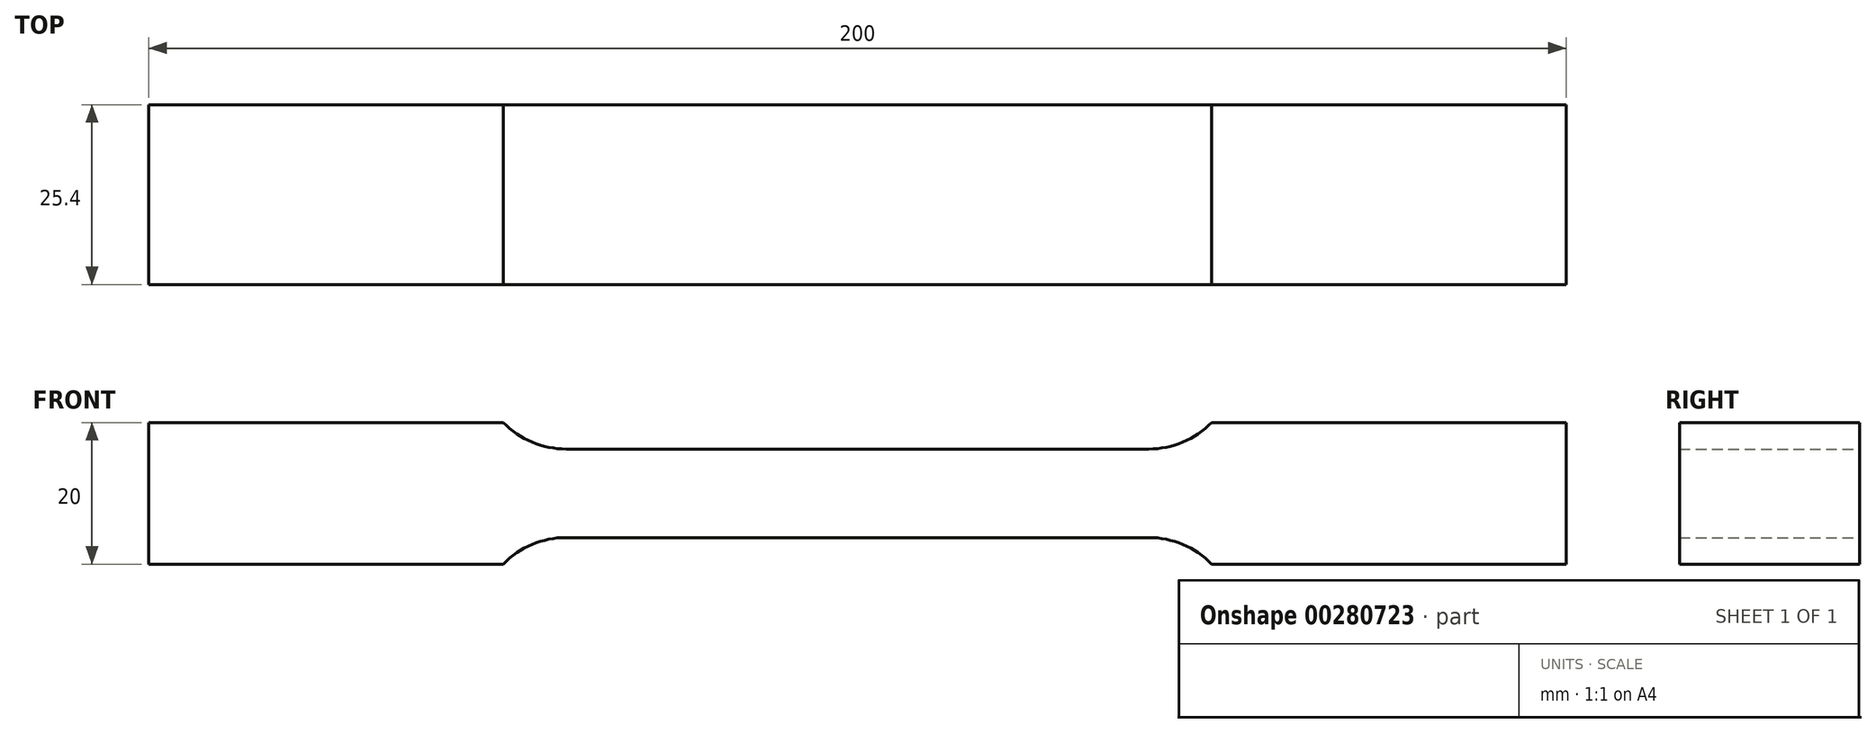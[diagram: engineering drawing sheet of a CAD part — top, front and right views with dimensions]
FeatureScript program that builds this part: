
annotation { "Feature Type Name" : "Feature", "Feature Type Description" : "" }
export const myFeature = defineFeature(function(context is Context, id is Id, definition is map)
    precondition{}
    {
        {
            var Q0;
            Q0=qCreatedBy(makeId("Front.planeOp"),FACE);
            var sketch = newSketch(context, id + "F0", { "sketchPlane" : qUnion([Q0])});
            skLineSegment(sketch, "E0", {"start": v(0, 6.25) * mm, "end": v(41.07, 6.25) * mm});
            skArc(sketch, "E1", {"start": v(41.07, 6.25) * mm, "mid": v(45.91, 7.23) * mm, "end": v(50, 10) * mm});
            skLineSegment(sketch, "E2", {"start": v(50, 10) * mm, "end": v(100, 10) * mm});
            skLineSegment(sketch, "E3.MirrorCS", {"start": v(0, -6.25) * mm, "end": v(41.07, -6.25) * mm});
            skLineSegment(sketch, "E4.MirrorCS", {"start": v(50, -10) * mm, "end": v(100, -10) * mm});
            skArc(sketch, "E5.MirrorCS", {"start": v(41.07, -6.25) * mm, "mid": v(45.91, -7.23) * mm, "end": v(50, -10) * mm});
            skLineSegment(sketch, "E6.MirrorCS", {"start": v(-50, 10) * mm, "end": v(-100, 10) * mm});
            skLineSegment(sketch, "E7.MirrorCS", {"start": v(-50, -10) * mm, "end": v(-100, -10) * mm});
            skArc(sketch, "E8.MirrorCS", {"start": v(-41.07, -6.25) * mm, "mid": v(-45.91, -7.23) * mm, "end": v(-50, -10) * mm});
            skLineSegment(sketch, "E9.MirrorCS", {"start": v(0, -6.25) * mm, "end": v(-41.07, -6.25) * mm});
            skLineSegment(sketch, "E10.MirrorCS", {"start": v(0, 6.25) * mm, "end": v(-41.07, 6.25) * mm});
            skArc(sketch, "E11.MirrorCS", {"start": v(-41.07, 6.25) * mm, "mid": v(-45.91, 7.23) * mm, "end": v(-50, 10) * mm});
            skLineSegment(sketch, "E12", {"start": v(-100, 10) * mm, "end": v(-100, -10) * mm});
            skLineSegment(sketch, "E13", {"start": v(100, 10) * mm, "end": v(100, -10) * mm});
            skSolve(sketch);
        }
        {
            var Q0;
            Q0 = qSketchRegion(id + "F0", true);
            extrude(context, id + "F1", {"entities" : qUnion([Q0]), "depth" : 25.4 * mm});
        }
    });
